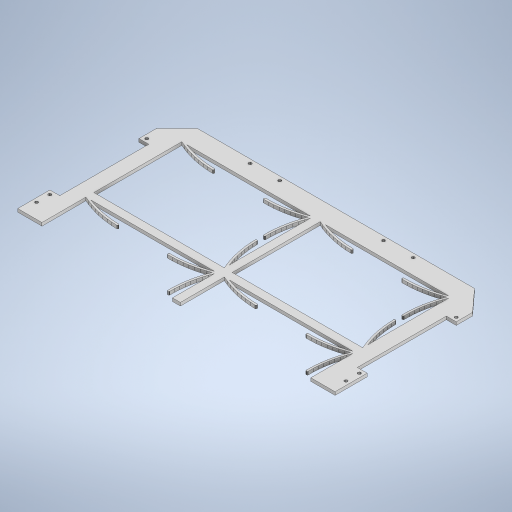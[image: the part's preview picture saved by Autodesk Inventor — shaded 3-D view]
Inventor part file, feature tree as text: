
AUTODESK INVENTOR PART (.ipt)
format: ipt  version: 2024.1 (Build 281209000, 209)  size: 936,960 bytes
history: native  units: in
note: dims shown in document units (in); Inventor stores cm internally (conversion verified against a paired STEP export)
features: extrude x1, sketch x1
ambient origin geometry x8: Origin, YZ Plane, XZ Plane, XY Plane, X Axis, Y Axis, Z Axis, Center Point
bodies: Solid1 (feature_tree)
feature tree (2):
  extrude  "Extrusion1"  [1 undecoded]
  sketch  "Sketch1"  dims[d0=0.125in d1=0.0in]
note: 1 required parameter value undecoded (feature->parameter linkage not recoverable at this tier; creation-order binding heuristic only, values carry confidence <= 0.55)
